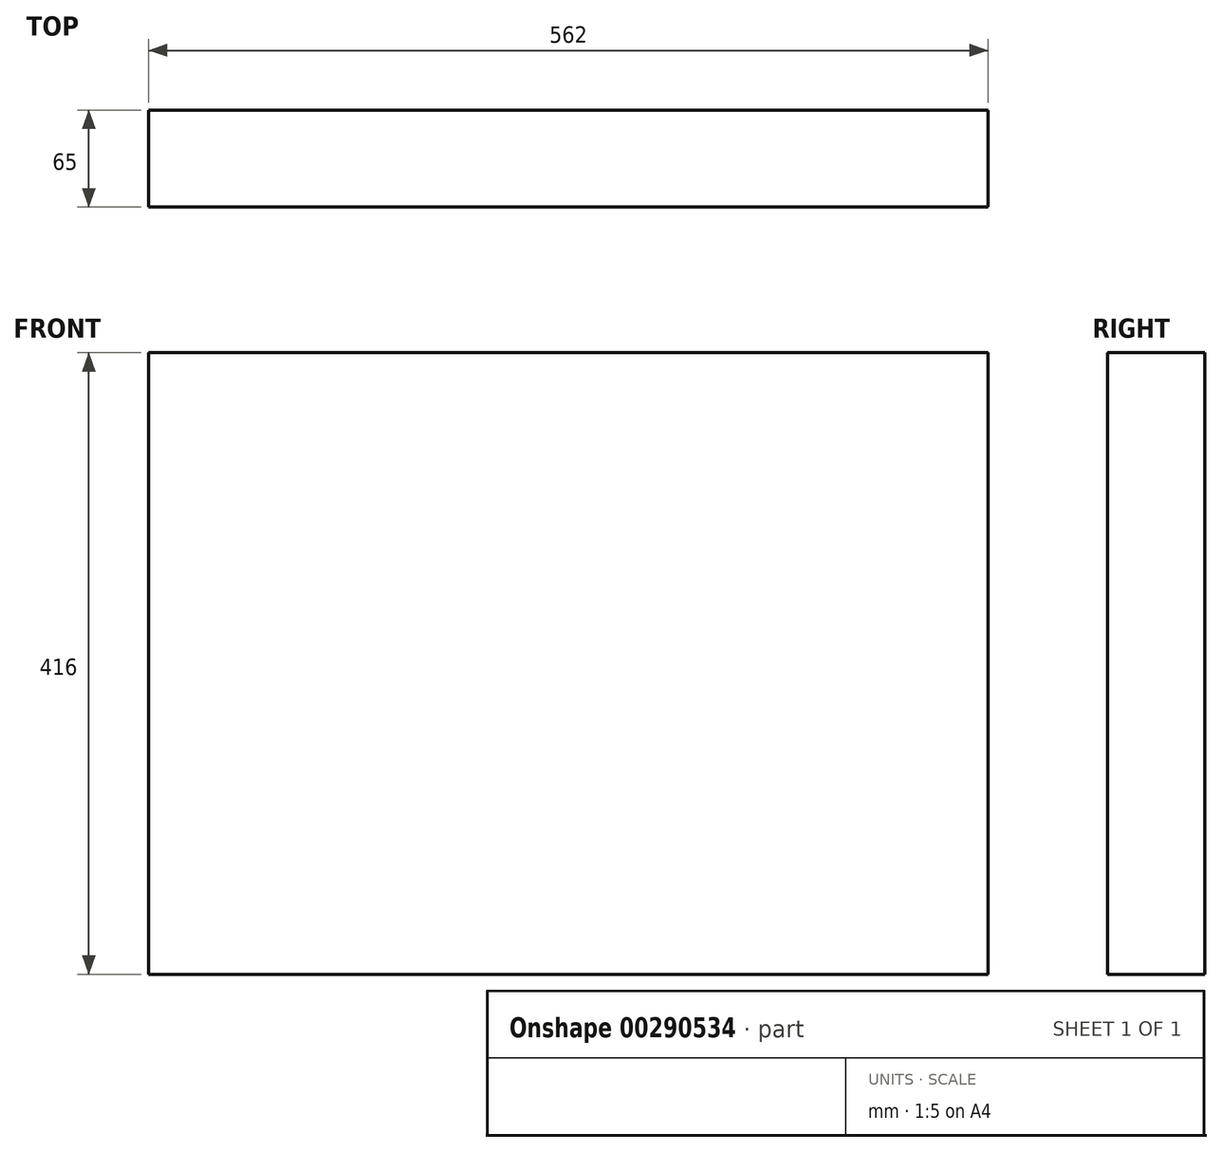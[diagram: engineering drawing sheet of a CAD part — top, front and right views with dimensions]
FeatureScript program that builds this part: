
annotation { "Feature Type Name" : "Feature", "Feature Type Description" : "" }
export const myFeature = defineFeature(function(context is Context, id is Id, definition is map)
    precondition{}
    {
        {
            var Q0;
            Q0=qCreatedBy(makeId("Front.planeOp"),FACE);
            var sketch = newSketch(context, id + "F0", { "sketchPlane" : qUnion([Q0])});
            skLineSegment(sketch, "E0.bottom", {"start": v(281, -208) * mm, "end": v(-281, -208) * mm});
            skLineSegment(sketch, "E0.top", {"start": v(281, 208) * mm, "end": v(-281, 208) * mm});
            skLineSegment(sketch, "E0.left", {"start": v(281, -208) * mm, "end": v(281, 208) * mm});
            skLineSegment(sketch, "E0.right", {"start": v(-281, -208) * mm, "end": v(-281, 208) * mm});
            skPoint(sketch, "E0.middle", {"position": v(0, 0) * mm});
            skSolve(sketch);
        }
        {
            var Q0;
            Q0 = qSketchRegion(id + "F0", true);
            extrude(context, id + "F1", {"entities" : qUnion([Q0]), "oppositeDirection" : true, "depth" : 65 * mm});
        }
    });
